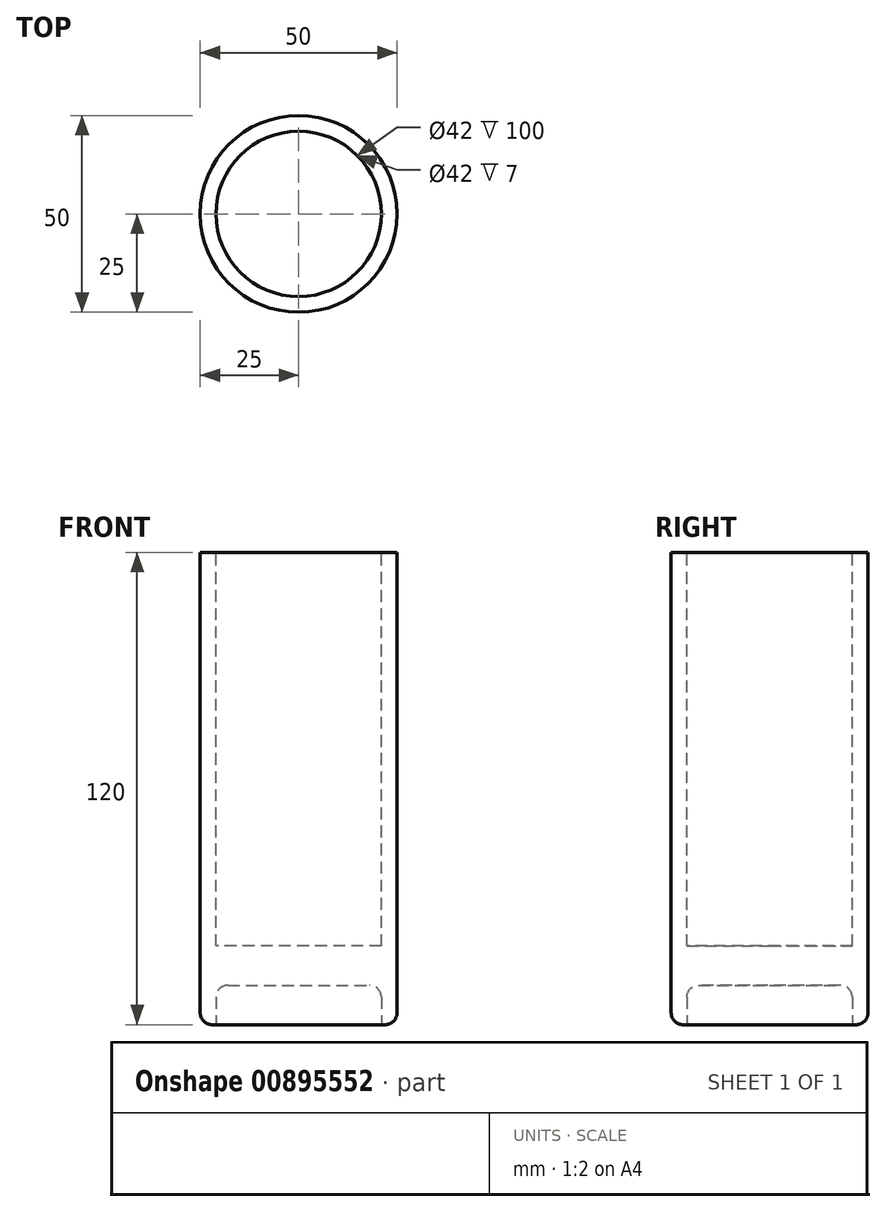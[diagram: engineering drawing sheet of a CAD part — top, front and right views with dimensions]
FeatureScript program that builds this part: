
annotation { "Feature Type Name" : "Feature", "Feature Type Description" : "" }
export const myFeature = defineFeature(function(context is Context, id is Id, definition is map)
    precondition{}
    {
        {
            var Q0;
            Q0=qCreatedBy(makeId("Top.planeOp"),FACE);
            var sketch = newSketch(context, id + "F0", { "sketchPlane" : qUnion([Q0])});
            skCircle(sketch, "E0", {"center": v(0, 0) * mm, "radius": 25 * mm});
            skSolve(sketch);
        }
        {
            var Q0;
            Q0=makeQuery(id+"F0.imprint","IMPRINT",FACE,{"disambiguationData":[TD([[makeQuery(id+"F0.imprint","IMPRINT",EDGE,{"derivedFrom":sQuery(id+"F0.wireOp",EDGE,"E0")}),1.0]])]});
            extrude(context, id + "F1", {"entities" : qUnion([Q0]), "depth" : 120 * mm, "offsetDistance" : 25 * mm});
        }
        {
            var Q0;
            Q0=makeQuery(id+"F1.opExtrude","CAP_FACE",FACE,{"disambiguationData":[OSD([sQuery(id+"F0.wireOp",EDGE,"E0")])],"isStart":false});
            var sketch = newSketch(context, id + "F2", { "sketchPlane" : qUnion([Q0])});
            skCircle(sketch, "E1", {"center": v(0, 0) * mm, "radius": 21 * mm});
            skSolve(sketch);
        }
        {
            var Q0;
            Q0 = qSketchRegion(id + "F2", true);
            extrude(context, id + "F3", {"entities" : qUnion([Q0]), "operationType" : NewBodyOperationType.REMOVE, "oppositeDirection" : true, "depth" : 100 * mm, "offsetDistance" : 25 * mm});
        }
        {
            var Q0;
            Q0=makeQuery(id+"F1.opExtrude","CAP_FACE",FACE,{"disambiguationData":[OSD([sQuery(id+"F0.wireOp",EDGE,"E0")])],"isStart":true});
            var sketch = newSketch(context, id + "F4", { "sketchPlane" : qUnion([Q0])});
            skCircle(sketch, "E2", {"center": v(0, 0) * mm, "radius": 21 * mm});
            skSolve(sketch);
        }
        {
            var Q0;
            Q0 = qSketchRegion(id + "F4", true);
            extrude(context, id + "F5", {"entities" : qUnion([Q0]), "operationType" : NewBodyOperationType.REMOVE, "oppositeDirection" : true, "depth" : 10 * mm, "offsetDistance" : 25 * mm});
        }
        {
            var Q0;
            Q0=makeQuery(id+"F1.opExtrude","CAP_EDGE",EDGE,{"disambiguationData":[OSD([sQuery(id+"F0.wireOp",EDGE,"E0")])],"isStart":true});
            var Q1;
            Q1=makeQuery(id+"F5.boolean.opBoolean","COPY",EDGE,{"derivedFrom":makeQuery(id+"F5.opExtrude","CAP_EDGE",EDGE,{"disambiguationData":[OSD([sQuery(id+"F4.wireOp",EDGE,"E2")])],"isStart":false})});
            fillet(context, id + "F6", {"entities" : qUnion([Q0, Q1]), "radius" : 3 * mm, "tangentPropagation" : true, "allowEdgeOverflow" : false});
        }
    });
